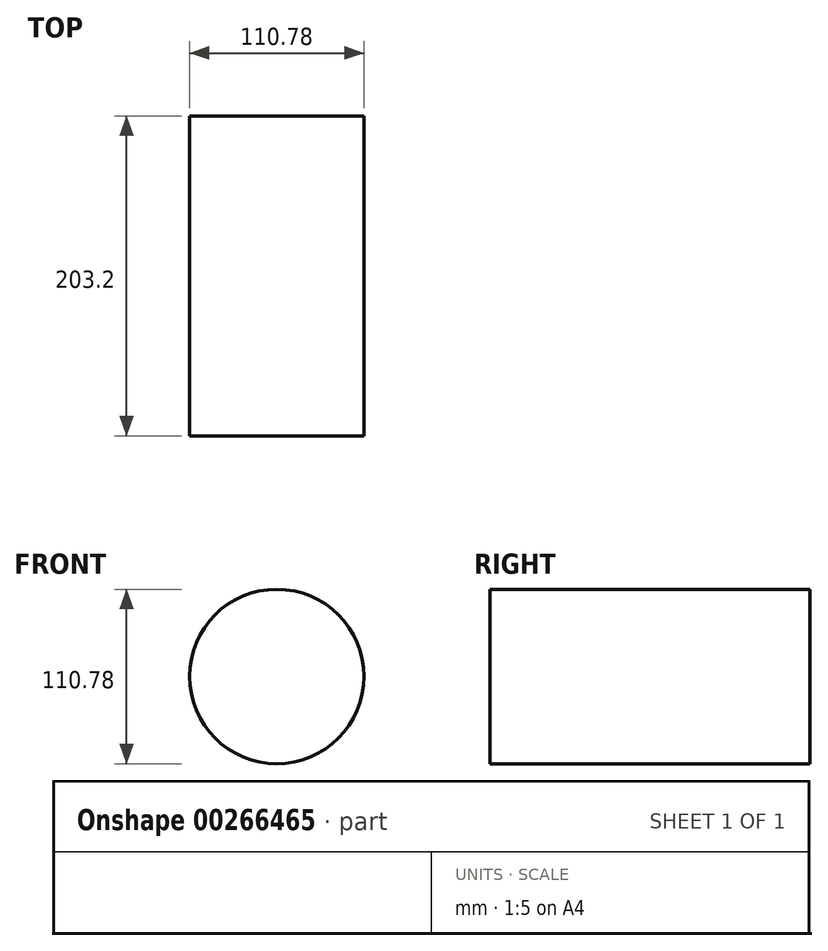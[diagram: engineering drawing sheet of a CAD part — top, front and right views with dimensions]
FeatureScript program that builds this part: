
annotation { "Feature Type Name" : "Feature", "Feature Type Description" : "" }
export const myFeature = defineFeature(function(context is Context, id is Id, definition is map)
    precondition{}
    {
        {
            var Q0;
            Q0=qCreatedBy(makeId("Front.planeOp"),FACE);
            var sketch = newSketch(context, id + "F0", { "sketchPlane" : qUnion([Q0])});
            skCircle(sketch, "E0", {"center": v(0, 0) * mm, "radius": 55.39 * mm});
            skSolve(sketch);
        }
        {
            var Q0;
            Q0 = qSketchRegion(id + "F0", true);
            extrude(context, id + "F1", {"entities" : qUnion([Q0]), "depth" : 203.2 * mm});
        }
    });
